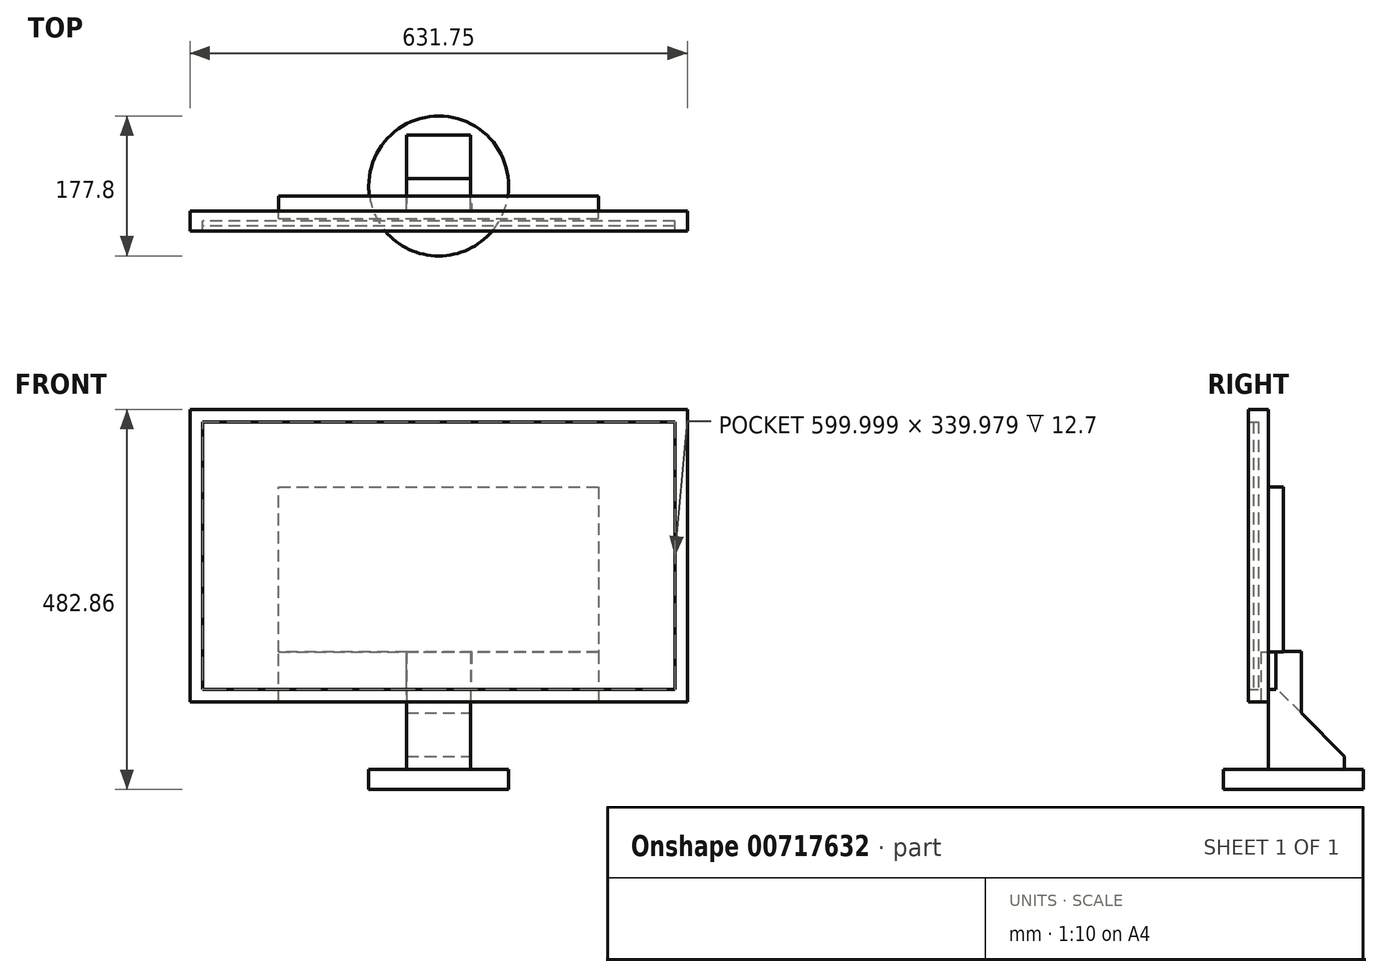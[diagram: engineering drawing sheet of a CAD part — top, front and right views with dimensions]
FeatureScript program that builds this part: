
annotation { "Feature Type Name" : "Feature", "Feature Type Description" : "" }
export const myFeature = defineFeature(function(context is Context, id is Id, definition is map)
    precondition{}
    {
        {
            var Q0;
            Q0=qCreatedBy(makeId("Front.planeOp"),FACE);
            var sketch = newSketch(context, id + "F0", { "sketchPlane" : qUnion([Q0])});
            skLineSegment(sketch, "E0.bottom", {"start": v(-325.58, 229.48) * mm, "end": v(306.17, 229.48) * mm});
            skLineSegment(sketch, "E0.top", {"start": v(-325.58, -142.25) * mm, "end": v(306.17, -142.25) * mm});
            skLineSegment(sketch, "E0.left", {"start": v(-325.58, 229.48) * mm, "end": v(-325.58, -142.25) * mm});
            skLineSegment(sketch, "E0.right", {"start": v(306.17, 229.48) * mm, "end": v(306.17, -142.25) * mm});
            skLineSegment(sketch, "E1", {"start": v(-309.7, 213.6) * mm, "end": v(-309.7, -126.38) * mm});
            skLineSegment(sketch, "E2", {"start": v(-309.7, -126.38) * mm, "end": v(290.3, -126.38) * mm});
            skLineSegment(sketch, "E3", {"start": v(290.3, -126.38) * mm, "end": v(290.3, 213.6) * mm});
            skLineSegment(sketch, "E4", {"start": v(290.3, 213.6) * mm, "end": v(-309.7, 213.6) * mm});
            skSolve(sketch);
        }
        {
            var Q0;
            Q0=makeQuery(id+"F0.imprint","IMPRINT",FACE,{"disambiguationData":[TD([[makeQuery(id+"F0.imprint","IMPRINT",EDGE,{"derivedFrom":sQuery(id+"F0.wireOp",EDGE,"E0.bottom")}),-1.0]])]});
            extrude(context, id + "F1", {"entities" : qUnion([Q0]), "depth" : 25.4 * mm});
        }
        {
            var Q0;
            Q0=makeQuery(id+"F0.imprint","IMPRINT",FACE,{"disambiguationData":[TD([[makeQuery(id+"F0.imprint","IMPRINT",EDGE,{"derivedFrom":sQuery(id+"F0.wireOp",EDGE,"E1")}),1.0]])]});
            extrude(context, id + "F2", {"entities" : qUnion([Q0]), "operationType" : NewBodyOperationType.ADD, "depth" : 12.7 * mm});
        }
        {
            var Q0;
            Q0=makeQuery(id+"F0.imprint","IMPRINT",FACE,{"disambiguationData":[TD([[makeQuery(id+"F0.imprint","IMPRINT",EDGE,{"derivedFrom":sQuery(id+"F0.wireOp",EDGE,"E1")}),1.0]])]});
            var sketch = newSketch(context, id + "F3", { "sketchPlane" : qUnion([Q0])});
            skLineSegment(sketch, "E5", {"start": v(-212.9, 130.8) * mm, "end": v(193.5, 130.8) * mm});
            skLineSegment(sketch, "E6", {"start": v(193.5, 130.8) * mm, "end": v(193.5, -78.75) * mm});
            skLineSegment(sketch, "E7", {"start": v(193.5, -78.75) * mm, "end": v(-212.9, -78.75) * mm});
            skLineSegment(sketch, "E8", {"start": v(-212.9, -78.75) * mm, "end": v(-212.9, 130.8) * mm});
            skSolve(sketch);
        }
        {
            var Q0;
            Q0=makeQuery(id+"F3.imprint","IMPRINT",FACE,{"disambiguationData":[TD([[makeQuery(id+"F3.imprint","IMPRINT",EDGE,{"derivedFrom":sQuery(id+"F3.wireOp",EDGE,"E5")}),-1.0]])]});
            extrude(context, id + "F4", {"entities" : qUnion([Q0]), "operationType" : NewBodyOperationType.ADD, "oppositeDirection" : true, "depth" : 19.05 * mm});
        }
        {
            var Q0;
            Q0=makeQuery(id+"F0.imprint","IMPRINT",FACE,{"disambiguationData":[TD([[makeQuery(id+"F0.imprint","IMPRINT",EDGE,{"derivedFrom":sQuery(id+"F0.wireOp",EDGE,"E1")}),1.0]])]});
            var sketch = newSketch(context, id + "F5", { "sketchPlane" : qUnion([Q0])});
            skPoint(sketch, "E9.0", {"position": v(193.5, -78.75) * mm});
            skPoint(sketch, "E10.0", {"position": v(-212.9, -78.75) * mm});
            skLineSegment(sketch, "E11", {"start": v(193.5, -78.75) * mm, "end": v(193.5, -142.25) * mm});
            skLineSegment(sketch, "E12", {"start": v(193.5, -142.25) * mm, "end": v(-212.9, -142.25) * mm});
            skLineSegment(sketch, "E13", {"start": v(-212.9, -142.25) * mm, "end": v(-212.9, -78.75) * mm});
            skLineSegment(sketch, "E14", {"start": v(-212.9, -78.75) * mm, "end": v(193.5, -78.75) * mm});
            skSolve(sketch);
        }
        {
            var Q0;
            {var subQ5=sQuery(id+"F5.wireOp",EDGE,"E12");Q0=makeQuery(id+"F5.imprint","IMPRINT",FACE,{"disambiguationData":[TD([[makeQuery(id+"F5.imprint","IMPRINT",EDGE,{"derivedFrom":subQ5}),-1.0]])]});}
            var Q1;
            {var subQ5=sQuery(id+"F5.wireOp",EDGE,"E14");Q1=makeQuery(id+"F5.imprint","IMPRINT",FACE,{"disambiguationData":[TD([[makeQuery(id+"F5.imprint","IMPRINT",EDGE,{"derivedFrom":subQ5}),-1.0]])]});}
            extrude(context, id + "F6", {"entities" : qUnion([Q0, Q1]), "operationType" : NewBodyOperationType.REMOVE, "depth" : 9.52 * mm});
        }
        {
            var Q0;
            {var subQ5=sQuery(id+"F5.wireOp",EDGE,"E14");Q0=makeQuery(id+"F5.imprint","IMPRINT",FACE,{"disambiguationData":[TD([[makeQuery(id+"F5.imprint","IMPRINT",EDGE,{"derivedFrom":subQ5}),-1.0]])]});}
            var sketch = newSketch(context, id + "F7", { "sketchPlane" : qUnion([Q0])});
            skLineSegment(sketch, "E15", {"start": v(31.57, -126.38) * mm, "end": v(-50.98, -126.38) * mm});
            skPoint(sketch, "E16.0", {"position": v(-212.9, -78.75) * mm});
            skLineSegment(sketch, "E17", {"start": v(-50.98, -78.75) * mm, "end": v(31.57, -78.75) * mm});
            skLineSegment(sketch, "E18", {"start": v(-50.98, -78.75) * mm, "end": v(-50.98, -126.38) * mm});
            skLineSegment(sketch, "E19", {"start": v(32, -78.67) * mm, "end": v(31.57, -126.38) * mm});
            skSolve(sketch);
        }
        {
            var Q0;
            {var subQ5=sQuery(id+"F7.wireOp",EDGE,"E15");Q0=makeQuery(id+"F7.imprint","IMPRINT",FACE,{"disambiguationData":[TD([[makeQuery(id+"F7.imprint","IMPRINT",EDGE,{"derivedFrom":subQ5}),1.0]])]});}
            extrude(context, id + "F8", {"entities" : qUnion([Q0]), "operationType" : NewBodyOperationType.ADD, "oppositeDirection" : true, "depth" : 9.52 * mm});
        }
        {
            var Q0;
            Q0=makeQuery(id+"F8.opExtrude","CAP_FACE",FACE,{"disambiguationData":[OSD([sQuery(id+"F5.wireOp",EDGE,"E14"),sQuery(id+"F7.wireOp",EDGE,"E15"),sQuery(id+"F7.wireOp",EDGE,"E17"),sQuery(id+"F7.wireOp",EDGE,"E18"),sQuery(id+"F7.wireOp",EDGE,"E19")])],"isStart":false});
            var sketch = newSketch(context, id + "F9", { "sketchPlane" : qUnion([Q0])});
            skLineSegment(sketch, "E20", {"start": v(-28.68, -94.63) * mm, "end": v(47.8, -94.63) * mm});
            skLineSegment(sketch, "E21", {"start": v(47.8, -94.63) * mm, "end": v(47.8, -126.38) * mm});
            skLineSegment(sketch, "E22", {"start": v(47.8, -126.38) * mm, "end": v(-28.68, -126.38) * mm});
            skLineSegment(sketch, "E23", {"start": v(-28.68, -94.63) * mm, "end": v(-28.68, -126.38) * mm});
            skSolve(sketch);
        }
        {
            var Q0;
            Q0=makeQuery(id+"F9.imprint","IMPRINT",FACE,{"disambiguationData":[TD([[makeQuery(id+"F9.imprint","IMPRINT",EDGE,{"derivedFrom":sQuery(id+"F9.wireOp",EDGE,"E20")}),-1.0]])]});
            extrude(context, id + "F10", {"entities" : qUnion([Q0]), "operationType" : NewBodyOperationType.ADD, "depth" : 44.45 * mm});
        }
        {
            var Q0;
            Q0=makeQuery(id+"F10.boolean.opBoolean","MERGE",FACE,{"derivedFrom":[makeQuery(id+"F8.opExtrude","SWEPT_FACE",FACE,{"disambiguationData":[OSD([sQuery(id+"F7.wireOp",EDGE,"E15")])]}),makeQuery(id+"F10.opExtrude","SWEPT_FACE",FACE,{"disambiguationData":[OSD([sQuery(id+"F9.wireOp",EDGE,"E22")])]})]});
            var sketch = newSketch(context, id + "F11", { "sketchPlane" : qUnion([Q0])});
            skLineSegment(sketch, "E24", {"start": v(28.68, -9.53) * mm, "end": v(-47.8, -9.53) * mm});
            skLineSegment(sketch, "E25", {"start": v(-47.8, -9.52) * mm, "end": v(-47.8, -53.98) * mm});
            skLineSegment(sketch, "E26", {"start": v(-47.8, -53.98) * mm, "end": v(28.68, -53.98) * mm});
            skLineSegment(sketch, "E27", {"start": v(28.68, -53.98) * mm, "end": v(28.68, -9.52) * mm});
            skSolve(sketch);
        }
        {
            var Q0;
            Q0=makeQuery(id+"F11.imprint","IMPRINT",FACE,{"disambiguationData":[TD([[makeQuery(id+"F11.imprint","IMPRINT",EDGE,{"derivedFrom":sQuery(id+"F11.wireOp",EDGE,"E24")}),1.0]])]});
            extrude(context, id + "F12", {"entities" : qUnion([Q0]), "operationType" : NewBodyOperationType.ADD, "depth" : 101.6 * mm});
        }
        {
            var Q0;
            Q0=makeQuery(id+"F12.opExtrude","CAP_FACE",FACE,{"disambiguationData":[OSD([sQuery(id+"F11.wireOp",EDGE,"E24"),sQuery(id+"F11.wireOp",EDGE,"E25"),sQuery(id+"F11.wireOp",EDGE,"E26"),sQuery(id+"F11.wireOp",EDGE,"E27")])],"isStart":false});
            var sketch = newSketch(context, id + "F13", { "sketchPlane" : qUnion([Q0])});
            skCircle(sketch, "E28", {"center": v(-9.56, -31.75) * mm, "radius": 88.9 * mm});
            skPoint(sketch, "E28.centerSnap0", {"position": v(-9.56, -53.98) * mm});
            skPoint(sketch, "E28.centerSnap1", {"position": v(28.68, -31.75) * mm});
            skSolve(sketch);
        }
        {
            var Q0;
            Q0=qSketchRegion(id+"F13",true);
            extrude(context, id + "F14", {"entities" : qUnion([Q0]), "operationType" : NewBodyOperationType.ADD, "depth" : 25.4 * mm});
        }
        {
            var Q0;
            Q0=makeQuery(id+"F12.boolean.opBoolean","MERGE",FACE,{"derivedFrom":[makeQuery(id+"F10.opExtrude","SWEPT_FACE",FACE,{"disambiguationData":[OSD([sQuery(id+"F9.wireOp",EDGE,"E21")])]}),makeQuery(id+"F12.opExtrude","SWEPT_FACE",FACE,{"disambiguationData":[OSD([sQuery(id+"F11.wireOp",EDGE,"E25")])]})]});
            var sketch = newSketch(context, id + "F15", { "sketchPlane" : qUnion([Q0])});
            skLineSegment(sketch, "E29.0", {"start": v(-15.88, -126.38) * mm, "end": v(-15.88, -100.98) * mm});
            skLineSegment(sketch, "E29.2", {"start": v(-47.62, -221.63) * mm, "end": v(-15.87, -221.63) * mm});
            skLineSegment(sketch, "E29.3", {"start": v(-47.62, -100.98) * mm, "end": v(-47.62, -221.63) * mm});
            skLineSegment(sketch, "E29.4", {"start": v(-15.88, -100.98) * mm, "end": v(-47.62, -100.98) * mm});
            skSolve(sketch);
        }
        {
            var Q0;
            {var subQ3=sQuery(id+"F15.wireOp",EDGE,"E29.3");Q0=makeQuery(id+"F15.imprint","IMPRINT",FACE,{"disambiguationData":[TD([[makeQuery(id+"F15.imprint","IMPRINT",EDGE,{"derivedFrom":subQ3}),1.0]])]});}
            var Q1;
            {var subQ8=sQuery(id+"F15.wireOp",EDGE,"E29.3");Q1=makeQuery(id+"F15.imprint","IMPRINT",FACE,{"disambiguationData":[TD([[makeQuery(id+"F15.imprint","IMPRINT",EDGE,{"derivedFrom":subQ8}),-1.0]])]});}
            var Q2;
            {var subQ1=sQuery(id+"F15.wireOp",EDGE,"ca770b93-93b2-40a0-9a67-044bb50748b5.0");var subQ3=sQuery(id+"F15.wireOp",EDGE,"E29.0");var subQ5=makeQuery(id+"F15.imprint","INTERSECT",VERTEX,{"derivedFrom":[subQ1,subQ3]});Q2=makeQuery(id+"F15.imprint","IMPRINT",FACE,{"disambiguationData":[TD([[makeQuery(id+"F15.imprint","IMPRINT",EDGE,{"disambiguationData":[TD([[subQ5,-1.0]])],"derivedFrom":subQ1}),1.0]])]});}
            var Q3;
            {var subQ0=sQuery(id+"F11.wireOp",EDGE,"E25");var subQ4=makeQuery(id+"F12.opExtrude","SWEPT_EDGE",EDGE,{"disambiguationData":[OSD([sQuery(id+"F7.wireOp",EDGE,"E15"),sQuery(id+"F11.wireOp",EDGE,"E24"),subQ0])]});Q3=makeQuery(id+"F15.imprint","IMPRINT",FACE,{"disambiguationData":[TD([[makeQuery(id+"F15.imprint","IMPRINT",EDGE,{"derivedFrom":subQ4}),1.0]])]});}
            var Q4;
            {var subQ1=sQuery(id+"F15.wireOp",EDGE,"ca770b93-93b2-40a0-9a67-044bb50748b5.0");var subQ3=sQuery(id+"F15.wireOp",EDGE,"E29.1");var subQ5=makeQuery(id+"F15.imprint","INTERSECT",VERTEX,{"disambiguationData":[OD(1.0)],"derivedFrom":[subQ1,subQ3]});Q4=makeQuery(id+"F15.imprint","IMPRINT",FACE,{"disambiguationData":[TD([[makeQuery(id+"F15.imprint","IMPRINT",EDGE,{"disambiguationData":[TD([[subQ5,-1.0]])],"derivedFrom":subQ1}),1.0]])]});}
            extrude(context, id + "F16", {"entities" : qUnion([Q0, Q1, Q2, Q3, Q4]), "operationType" : NewBodyOperationType.REMOVE, "endBound" : BoundingType.UP_TO_NEXT, "oppositeDirection" : true, "depth" : 25.4 * mm});
        }
        {
            var Q0;
            Q0=makeQuery(id+"F2.opExtrude","CAP_FACE",FACE,{"disambiguationData":[OSD([sQuery(id+"F0.wireOp",EDGE,"E1"),sQuery(id+"F0.wireOp",EDGE,"E2"),sQuery(id+"F0.wireOp",EDGE,"E3"),sQuery(id+"F0.wireOp",EDGE,"E4")])],"isStart":false});
            extrude(context, id + "F17", {"entities" : qUnion([Q0]), "depth" : 6.35 * mm});
        }
        {
            var Q0;
            Q0=qCreatedBy(makeId("Front.planeOp"),FACE);
            var sketch = newSketch(context, id + "F18", { "sketchPlane" : qUnion([Q0])});
            skLineSegment(sketch, "E30.bottom", {"start": v(30.87, -79.17) * mm, "end": v(-50.28, -79.17) * mm});
            skLineSegment(sketch, "E30.top", {"start": v(30.87, -227.84) * mm, "end": v(-50.28, -227.84) * mm});
            skLineSegment(sketch, "E30.left", {"start": v(30.87, -79.17) * mm, "end": v(30.87, -227.84) * mm});
            skLineSegment(sketch, "E30.right", {"start": v(-50.28, -79.17) * mm, "end": v(-50.28, -227.84) * mm});
            skSolve(sketch);
        }
        {
            var Q0;
            Q0=makeQuery(id+"F18.imprint","IMPRINT",FACE,{"disambiguationData":[TD([[makeQuery(id+"F18.imprint","IMPRINT",EDGE,{"derivedFrom":sQuery(id+"F18.wireOp",EDGE,"E30.bottom")}),1.0]])]});
            extrude(context, id + "F19", {"entities" : qUnion([Q0]), "operationType" : NewBodyOperationType.ADD, "oppositeDirection" : true, "depth" : 96.52 * mm, "offsetDistance" : 25.4 * mm});
        }
        {
            var Q0;
            Q0=makeQuery(id+"F19.opExtrude","CAP_EDGE",EDGE,{"disambiguationData":[OSD([sQuery(id+"F18.wireOp",EDGE,"E30.bottom")])],"isStart":false});
            chamfer(context, id + "F20", {"entities" : qUnion([Q0]), "width" : 132.08 * mm, "tangentPropagation" : true});
        }
        {
            var Q0;
            Q0=makeQuery(id+"F19.opExtrude","SWEPT_FACE",FACE,{"disambiguationData":[OSD([sQuery(id+"F18.wireOp",EDGE,"E30.left")])]});
            var sketch = newSketch(context, id + "F21", { "sketchPlane" : qUnion([Q0])});
            skLineSegment(sketch, "E31.bottom", {"start": v(0, -78.22) * mm, "end": v(41.45, -78.22) * mm});
            skLineSegment(sketch, "E31.top", {"start": v(0, -227.84) * mm, "end": v(41.45, -227.84) * mm});
            skLineSegment(sketch, "E31.left", {"start": v(0, -78.22) * mm, "end": v(0, -227.84) * mm});
            skLineSegment(sketch, "E31.right", {"start": v(41.45, -78.22) * mm, "end": v(41.45, -227.84) * mm});
            skSolve(sketch);
        }
        {
            var Q0;
            {var subQ1=sQuery(id+"F21.wireOp",EDGE,"E31.bottom");Q0=makeQuery(id+"F21.imprint","IMPRINT",FACE,{"disambiguationData":[TD([[makeQuery(id+"F21.imprint","IMPRINT",EDGE,{"derivedFrom":subQ1}),-1.0]])]});}
            extrude(context, id + "F22", {"entities" : qUnion([Q0]), "operationType" : NewBodyOperationType.ADD, "oppositeDirection" : true, "depth" : 81.03 * mm, "offsetDistance" : 25.4 * mm});
        }
    });
